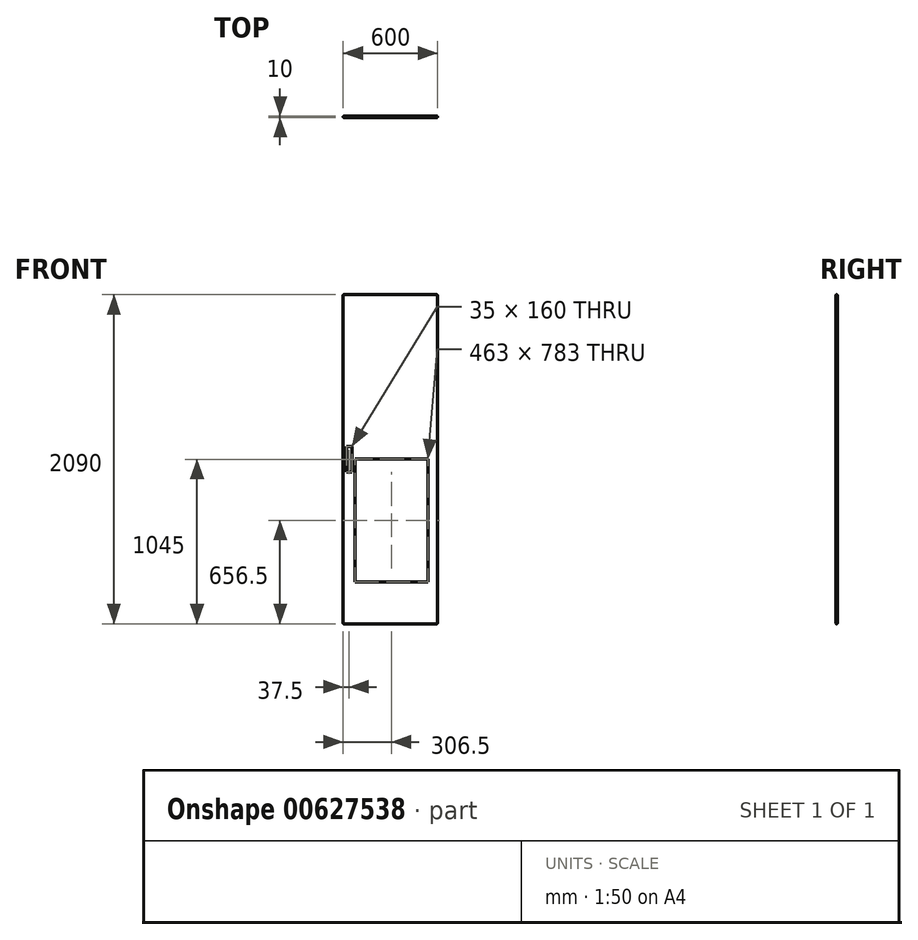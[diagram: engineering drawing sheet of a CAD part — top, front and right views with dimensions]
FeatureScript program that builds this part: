
annotation { "Feature Type Name" : "Feature", "Feature Type Description" : "" }
export const myFeature = defineFeature(function(context is Context, id is Id, definition is map)
    precondition{}
    {
        {
            var Q0;
            Q0=qCreatedBy(makeId("Front.planeOp"),FACE);
            var sketch = newSketch(context, id + "F0", { "sketchPlane" : qUnion([Q0])});
            skLineSegment(sketch, "E0.bottom", {"start": v(-300, 1045) * mm, "end": v(300, 1045) * mm});
            skLineSegment(sketch, "E0.top", {"start": v(-300, -1045) * mm, "end": v(300, -1045) * mm});
            skLineSegment(sketch, "E0.left", {"start": v(-300, 1045) * mm, "end": v(-300, -1045) * mm});
            skLineSegment(sketch, "E0.right", {"start": v(300, 1045) * mm, "end": v(300, -1045) * mm});
            skLineSegment(sketch, "E1.bottom", {"start": v(-225, 3) * mm, "end": v(238, 3) * mm});
            skLineSegment(sketch, "E1.top", {"start": v(-225, -780) * mm, "end": v(238, -780) * mm});
            skLineSegment(sketch, "E1.left", {"start": v(-225, 3) * mm, "end": v(-225, -780) * mm});
            skLineSegment(sketch, "E1.right", {"start": v(238, 3) * mm, "end": v(238, -780) * mm});
            skLineSegment(sketch, "E2.bottom", {"start": v(-280, 80) * mm, "end": v(-245, 80) * mm});
            skLineSegment(sketch, "E2.top", {"start": v(-280, -80) * mm, "end": v(-245, -80) * mm});
            skLineSegment(sketch, "E2.left", {"start": v(-280, 80) * mm, "end": v(-280, -80) * mm});
            skLineSegment(sketch, "E2.right", {"start": v(-245, 80) * mm, "end": v(-245, -80) * mm});
            skSolve(sketch);
        }
        {
            var Q0;
            Q0 = qSketchRegion(id + "F0", true);
            extrude(context, id + "F1", {"entities" : qUnion([Q0]), "depth" : 10 * mm, "offsetDistance" : 25 * mm});
        }
        {
            var Q0;
            Q0=makeQuery(id+"F1.opExtrude","SWEPT_EDGE",EDGE,{"disambiguationData":[OSD([sQuery(id+"F0.wireOp",EDGE,"E0.bottom"),sQuery(id+"F0.wireOp",EDGE,"E0.right")])]});
            var Q1;
            Q1=makeQuery(id+"F1.opExtrude","SWEPT_EDGE",EDGE,{"disambiguationData":[OSD([sQuery(id+"F0.wireOp",EDGE,"E0.bottom"),sQuery(id+"F0.wireOp",EDGE,"E0.left")])]});
            var Q2;
            Q2=makeQuery(id+"F1.opExtrude","SWEPT_EDGE",EDGE,{"disambiguationData":[OSD([sQuery(id+"F0.wireOp",EDGE,"E0.top"),sQuery(id+"F0.wireOp",EDGE,"E0.left")])]});
            var Q3;
            Q3=makeQuery(id+"F1.opExtrude","SWEPT_EDGE",EDGE,{"disambiguationData":[OSD([sQuery(id+"F0.wireOp",EDGE,"E0.top"),sQuery(id+"F0.wireOp",EDGE,"E0.right")])]});
            var Q4;
            Q4=makeQuery(id+"F1.opExtrude","CAP_EDGE",EDGE,{"disambiguationData":[OSD([sQuery(id+"F0.wireOp",EDGE,"E0.top")])],"isStart":false});
            var Q5;
            Q5=makeQuery(id+"F1.opExtrude","CAP_EDGE",EDGE,{"disambiguationData":[OSD([sQuery(id+"F0.wireOp",EDGE,"E0.left")])],"isStart":false});
            var Q6;
            Q6=makeQuery(id+"F1.opExtrude","CAP_EDGE",EDGE,{"disambiguationData":[OSD([sQuery(id+"F0.wireOp",EDGE,"E0.left")])],"isStart":true});
            var Q7;
            Q7=makeQuery(id+"F1.opExtrude","CAP_EDGE",EDGE,{"disambiguationData":[OSD([sQuery(id+"F0.wireOp",EDGE,"E0.top")])],"isStart":true});
            var Q8;
            Q8=makeQuery(id+"F1.opExtrude","CAP_EDGE",EDGE,{"disambiguationData":[OSD([sQuery(id+"F0.wireOp",EDGE,"E0.right")])],"isStart":true});
            var Q9;
            Q9=makeQuery(id+"F1.opExtrude","CAP_EDGE",EDGE,{"disambiguationData":[OSD([sQuery(id+"F0.wireOp",EDGE,"E0.right")])],"isStart":false});
            var Q10;
            Q10=makeQuery(id+"F1.opExtrude","CAP_EDGE",EDGE,{"disambiguationData":[OSD([sQuery(id+"F0.wireOp",EDGE,"E0.bottom")])],"isStart":false});
            var Q11;
            Q11=makeQuery(id+"F1.opExtrude","CAP_EDGE",EDGE,{"disambiguationData":[OSD([sQuery(id+"F0.wireOp",EDGE,"E0.bottom")])],"isStart":true});
            fillet(context, id + "F2", {"entities" : qUnion([Q0, Q1, Q2, Q3, Q4, Q5, Q6, Q7, Q8, Q9, Q10, Q11]), "radius" : 5 * mm, "tangentPropagation" : true, "allowEdgeOverflow" : false});
        }
    });
